# Revit family: Univers-IP41-empty-Surface_mounted-NoHosted-CH-en
name_source: partatom
category: Electrical Equipment
units: mm (PartAtom-declared; Revit-internal decimal feet)

## family parameters
Always vertical = Yes
Cut with Voids When Loaded = No
Panel Configuration = Two Columns, Circuits Across
Part Type = Panelboard
Room Calculation Point = No
Round Connector Dimension = Use Diameter
Shared = No
Work Plane-Based = Yes

## types (3) — shared parameters
Default Elevation = 1219 mm
EF000003 - Mounting method = EV000384 - Surface mounted (plaster)
EF000007 - Colour = EV000202 - White
EF000116 - RAL-number = 9010
EF000118 - With mounting plate = No
EF000218 - Built-in depth = 84 mm  [stored 0.275591 ft]
EF000339 - Type of cover = EV004216 - Door
EF001062 - EMC-version = No
EF001088 - Extension possible = No
EF001131 - Internal depth = 84 mm  [stored 0.275591 ft]
EF001134 - DIN-rail = No
EF001596 - Material housing = EV000154 - Other
EF005474 - Degree of protection (IP) = EV006416 - IP41
EF006244 - Transparent cover/door = No
EF006306 - With lock = No
EF009212 - Cover model = EV000116 - Closed
EF015776 - Earthing terminal block = No
EF015777 - Neutral terminal block = No
EF015941 - Signal passing door = No
HG000002 - With door or cover = Yes
HG000003 - Range = Univers
HG000005 - Thickness = 3 mm  [stored 0.00984252 ft]
HG000006 - Flush mounted = No
HG000009 - Double swing door = No
HG000010 - Asymmetric doors = No
HG000011 - Empty rows from bottom = No
Manufacturer = Hager
Type Comments = Univers
zero-valued in all types: EF000266 - Number of rows, EF000332 - Built-in height, EF002950 - Width in number of modular spacings, HG000001 - Number of columns, HG000007 - Number of empty columns, HG000008 - Number of empty rows

## per-type parameters (varying)
| type | EF000008 - Width | EF000040 - Height | EF000049 - Depth | EF000846 - Built-in width | EF004462 - Type of closure | HG000004 - Manufacturer reference | Model |
| Surface mounted IP41 W350 H350 D128 0 Modular spacings - FB2008LN | 350 mm | 350 mm | 128 mm | 200 mm  [stored 0.656168 ft] | EV000154 - Other | FB2008LN | FB2008LN |
| Surface mounted IP41 W450 H450 D128 0 Modular spacings - FB3008LN | 450 mm  [stored 1.47638 ft] | 450 mm  [stored 1.47638 ft] | 128 mm | 300 mm | EV000154 - Other | FB3008LN | FB3008LN |
| Surface mounted IP41 W540 H450 D148 0 Modular spacings - FB3008SN | 540 mm  [stored 1.77165 ft] | 450 mm  [stored 1.47638 ft] | 148 mm  [stored 0.485564 ft] | 300 mm | 0 | FB3008SN | FB3008SN |

note: [stored X ft] marks values corroborated as IEEE doubles in the binary element streams (Revit-internal decimal feet)

## geometry (parser evidence)
native form markers: Sweep x16
no freeform markers — native parametric forms only
